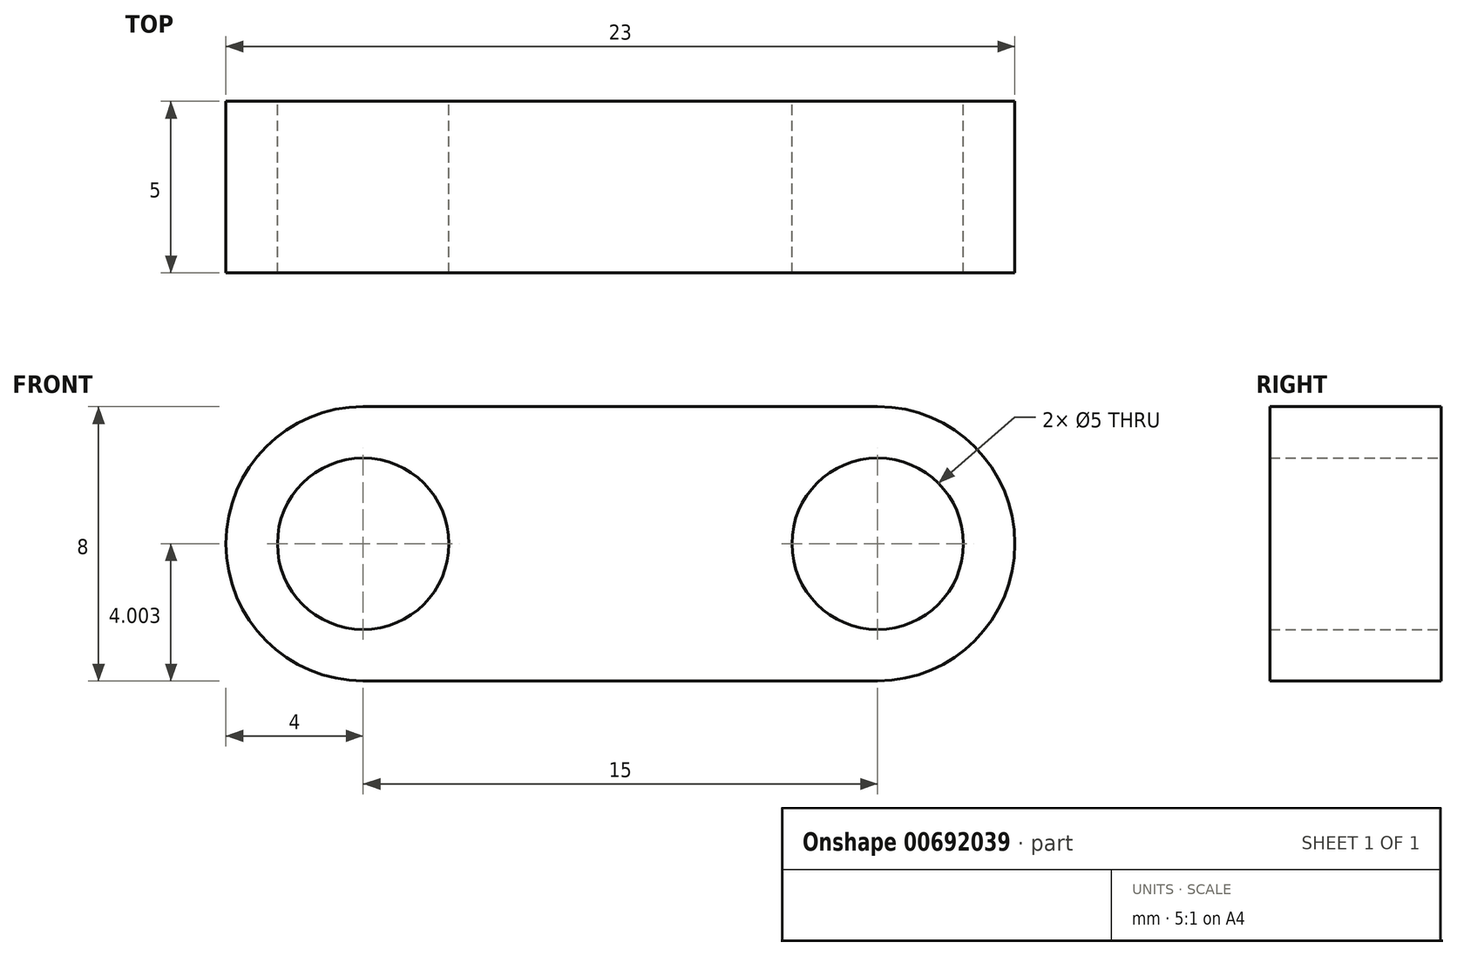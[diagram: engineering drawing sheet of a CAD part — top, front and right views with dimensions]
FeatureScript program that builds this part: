
annotation { "Feature Type Name" : "Feature", "Feature Type Description" : "" }
export const myFeature = defineFeature(function(context is Context, id is Id, definition is map)
    precondition{}
    {
        {
            var Q0;
            Q0=qCreatedBy(makeId("Front.planeOp"),FACE);
            var sketch = newSketch(context, id + "F0", { "sketchPlane" : qUnion([Q0])});
            skLineSegment(sketch, "E0.bottom", {"start": v(-8.73, 2.52) * mm, "end": v(6.27, 2.52) * mm});
            skLineSegment(sketch, "E0.top", {"start": v(-8.73, -5.48) * mm, "end": v(6.27, -5.48) * mm});
            skArc(sketch, "E1", {"start": v(-8.73, 2.52) * mm, "mid": v(-12.73, -1.48) * mm, "end": v(-8.73, -5.48) * mm});
            skArc(sketch, "E2", {"start": v(6.27, -5.48) * mm, "mid": v(10.27, -1.48) * mm, "end": v(6.27, 2.52) * mm});
            skCircle(sketch, "E3", {"center": v(-8.73, -1.48) * mm, "radius": 2.5 * mm});
            skCircle(sketch, "E4", {"center": v(6.27, -1.48) * mm, "radius": 2.5 * mm});
            skSolve(sketch);
        }
        {
            var Q0;
            Q0=makeQuery(id+"F0.imprint","IMPRINT",FACE,{"disambiguationData":[TD([[makeQuery(id+"F0.imprint","IMPRINT",EDGE,{"derivedFrom":sQuery(id+"F0.wireOp",EDGE,"E0.bottom")}),-1.0]])]});
            extrude(context, id + "F1", {"entities" : qUnion([Q0]), "depth" : 5 * mm, "offsetDistance" : 25 * mm});
        }
    });
